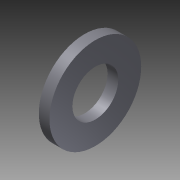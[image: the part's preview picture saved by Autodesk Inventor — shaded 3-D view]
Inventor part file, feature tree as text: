
AUTODESK INVENTOR PART (.ipt)
format: ipt  version: 2014 (Build 180170000, 170)  size: 98,816 bytes
history: native  units: mm (DEFAULTED — no unit token found)
features: other x1, plane x1, sketch x1
ambient origin geometry x7: Origin, YZ Plane, XY Plane, X Axis, Y Axis, Z Axis, Center Point
bodies: Solid1 (feature_tree), Body (feature_tree)
feature tree (3):
  other  "Work Axis1"
  plane  "Work Plane1"
  sketch  "Sketch"  dims[d0=8.7376mm d1=17.4752mm d2=2.032mm d3=0.0mm d4=0.0mm d5=0.0mm d6=0.0mm d7=0.0mm]
